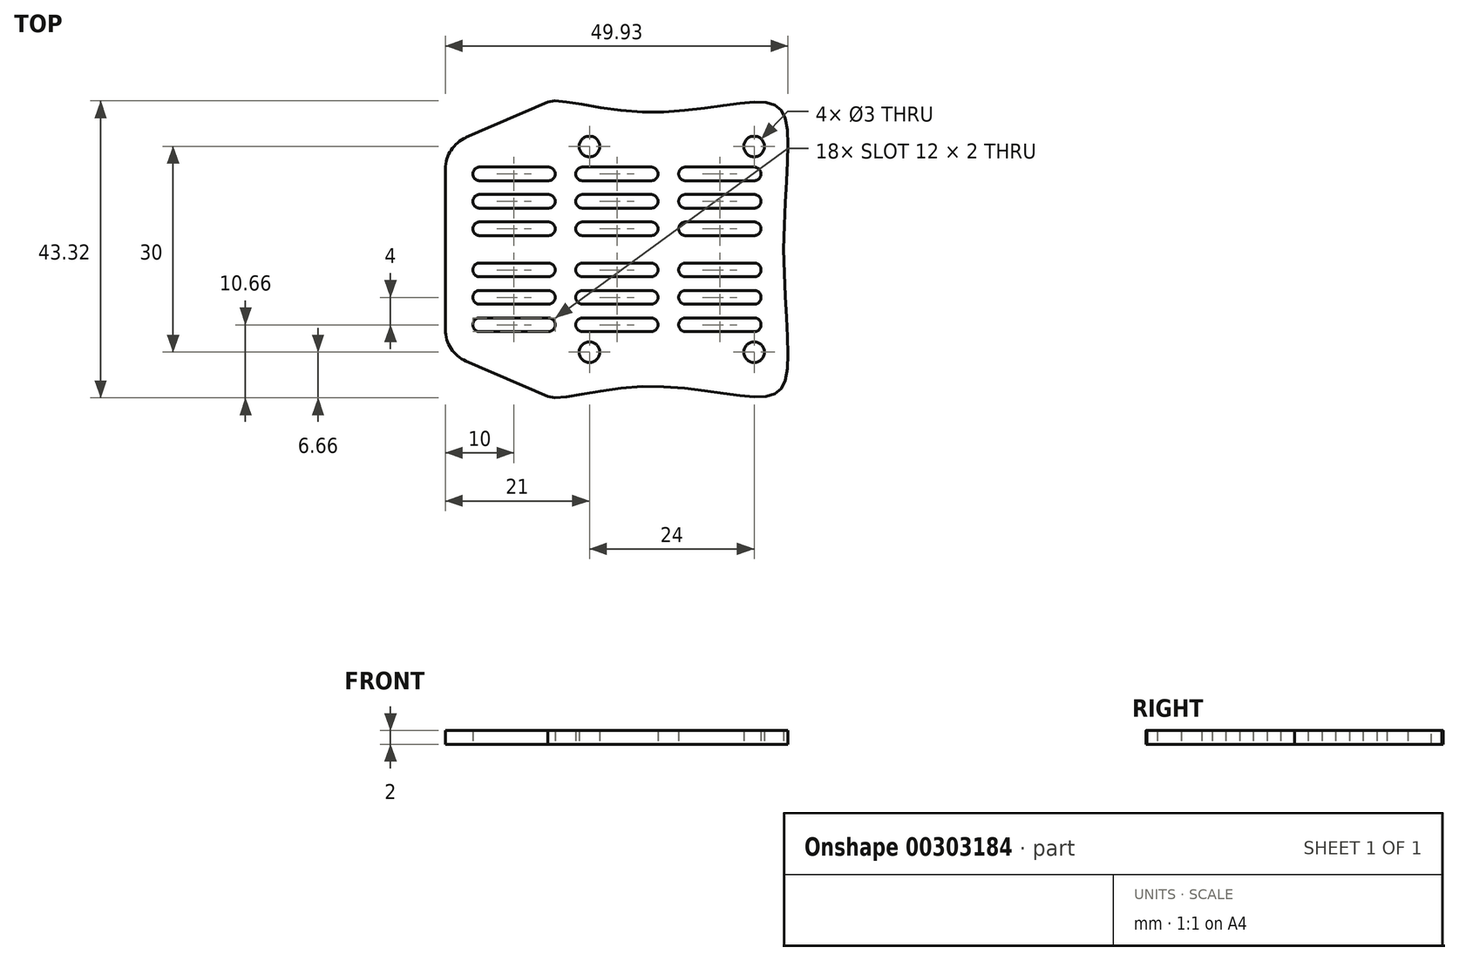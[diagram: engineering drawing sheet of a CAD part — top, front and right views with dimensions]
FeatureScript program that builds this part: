
annotation { "Feature Type Name" : "Feature", "Feature Type Description" : "" }
export const myFeature = defineFeature(function(context is Context, id is Id, definition is map)
    precondition{}
    {
        {
            var Q0;
            Q0=qCreatedBy(makeId("Top.planeOp"),FACE);
            var sketch = newSketch(context, id + "F0", { "sketchPlane" : qUnion([Q0])});
            skLineSegment(sketch, "E0", {"start": v(0, 0) * mm, "end": v(0, -11.72) * mm});
            skLineSegment(sketch, "E1", {"start": v(3.01, -16.3) * mm, "end": v(14.91, -21.46) * mm});
            skPoint(sketch, "E2.visualSharp", {"position": v(0, -15) * mm});
            skArc(sketch, "E2.filletArc", {"start": v(0, -11.72) * mm, "mid": v(0.82, -14.46) * mm, "end": v(3.01, -16.3) * mm});
            skCircle(sketch, "E3", {"center": v(45, -15) * mm, "radius": 1.5 * mm});
            skCircle(sketch, "E4", {"center": v(21, -15) * mm, "radius": 1.5 * mm});
            skLineSegment(sketch, "E5", {"start": v(0, -20) * mm, "end": v(69.47, -20) * mm, "construction": true});
            skLineSegment(sketch, "E6.MirrorCS", {"start": v(0, 20) * mm, "end": v(69.47, 20) * mm, "construction": true});
            skFitSpline(sketch, "E7", {"points": [v(14.91, -21.46) * mm, v(28.67, -20) * mm, v(46.46, -21.46) * mm, v(49.49, -19.15) * mm, v(49.31, 0) * mm], "startDerivative": vector(14.2, -9.6) * mm, "endDerivative": vector(-0.82, 81.71) * mm});
            skLineSegment(sketch, "E8.MirrorCS", {"start": v(0, 0) * mm, "end": v(0, 11.72) * mm});
            skArc(sketch, "E9.MirrorCS", {"start": v(0, 11.72) * mm, "mid": v(0.82, 14.46) * mm, "end": v(3.01, 16.3) * mm});
            skLineSegment(sketch, "E10.MirrorCS", {"start": v(3.01, 16.3) * mm, "end": v(14.91, 21.46) * mm});
            skFitSpline(sketch, "E11.MirrorCS", {"points": [v(14.91, 21.46) * mm, v(28.67, 20) * mm, v(46.46, 21.46) * mm, v(49.49, 19.15) * mm, v(49.31, 0) * mm], "startDerivative": vector(14.2, 9.6) * mm, "endDerivative": vector(-0.82, -81.71) * mm});
            skCircle(sketch, "E12.MirrorC", {"center": v(45, 15) * mm, "radius": 1.5 * mm});
            skCircle(sketch, "E13.MirrorC", {"center": v(21, 15) * mm, "radius": 1.5 * mm});
            skLineSegment(sketch, "E14", {"start": v(5, -3) * mm, "end": v(15, -3) * mm, "construction": true});
            skArc(sketch, "E15.0.startCap", {"start": v(5, -4) * mm, "mid": v(4, -3) * mm, "end": v(5, -2) * mm});
            skArc(sketch, "E15.0.endCap", {"start": v(15, -2) * mm, "mid": v(16, -3) * mm, "end": v(15, -4) * mm});
            skLineSegment(sketch, "E15.0.left", {"start": v(5, -2) * mm, "end": v(15, -2) * mm});
            skLineSegment(sketch, "E15.0.right", {"start": v(5, -4) * mm, "end": v(15, -4) * mm});
            skLineSegment(sketch, "E16.0.1.0", {"start": v(5, -8) * mm, "end": v(15, -8) * mm});
            skArc(sketch, "E16.0.1.1", {"start": v(15, -6) * mm, "mid": v(16, -7) * mm, "end": v(15, -8) * mm});
            skLineSegment(sketch, "E16.0.1.2", {"start": v(5, -6) * mm, "end": v(15, -6) * mm});
            skArc(sketch, "E16.0.1.3", {"start": v(5, -8) * mm, "mid": v(4, -7) * mm, "end": v(5, -6) * mm});
            skLineSegment(sketch, "E16.0.2.0", {"start": v(5, -12) * mm, "end": v(15, -12) * mm});
            skArc(sketch, "E16.0.2.1", {"start": v(15, -10) * mm, "mid": v(16, -11) * mm, "end": v(15, -12) * mm});
            skLineSegment(sketch, "E16.0.2.2", {"start": v(5, -10) * mm, "end": v(15, -10) * mm});
            skArc(sketch, "E16.0.2.3", {"start": v(5, -12) * mm, "mid": v(4, -11) * mm, "end": v(5, -10) * mm});
            skLineSegment(sketch, "E16.1.0.0", {"start": v(20, -4) * mm, "end": v(30, -4) * mm});
            skArc(sketch, "E16.1.0.1", {"start": v(30, -2) * mm, "mid": v(31, -3) * mm, "end": v(30, -4) * mm});
            skLineSegment(sketch, "E16.1.0.2", {"start": v(20, -2) * mm, "end": v(30, -2) * mm});
            skArc(sketch, "E16.1.0.3", {"start": v(20, -4) * mm, "mid": v(19, -3) * mm, "end": v(20, -2) * mm});
            skLineSegment(sketch, "E16.1.1.0", {"start": v(20, -8) * mm, "end": v(30, -8) * mm});
            skArc(sketch, "E16.1.1.1", {"start": v(30, -6) * mm, "mid": v(31, -7) * mm, "end": v(30, -8) * mm});
            skLineSegment(sketch, "E16.1.1.2", {"start": v(20, -6) * mm, "end": v(30, -6) * mm});
            skArc(sketch, "E16.1.1.3", {"start": v(20, -8) * mm, "mid": v(19, -7) * mm, "end": v(20, -6) * mm});
            skLineSegment(sketch, "E16.1.2.0", {"start": v(20, -12) * mm, "end": v(30, -12) * mm});
            skArc(sketch, "E16.1.2.1", {"start": v(30, -10) * mm, "mid": v(31, -11) * mm, "end": v(30, -12) * mm});
            skLineSegment(sketch, "E16.1.2.2", {"start": v(20, -10) * mm, "end": v(30, -10) * mm});
            skArc(sketch, "E16.1.2.3", {"start": v(20, -12) * mm, "mid": v(19, -11) * mm, "end": v(20, -10) * mm});
            skLineSegment(sketch, "E16.2.0.0", {"start": v(35, -4) * mm, "end": v(45, -4) * mm});
            skArc(sketch, "E16.2.0.1", {"start": v(45, -2) * mm, "mid": v(46, -3) * mm, "end": v(45, -4) * mm});
            skLineSegment(sketch, "E16.2.0.2", {"start": v(35, -2) * mm, "end": v(45, -2) * mm});
            skArc(sketch, "E16.2.0.3", {"start": v(35, -4) * mm, "mid": v(34, -3) * mm, "end": v(35, -2) * mm});
            skLineSegment(sketch, "E16.2.1.0", {"start": v(35, -8) * mm, "end": v(45, -8) * mm});
            skArc(sketch, "E16.2.1.1", {"start": v(45, -6) * mm, "mid": v(46, -7) * mm, "end": v(45, -8) * mm});
            skLineSegment(sketch, "E16.2.1.2", {"start": v(35, -6) * mm, "end": v(45, -6) * mm});
            skArc(sketch, "E16.2.1.3", {"start": v(35, -8) * mm, "mid": v(34, -7) * mm, "end": v(35, -6) * mm});
            skLineSegment(sketch, "E16.2.2.0", {"start": v(35, -12) * mm, "end": v(45, -12) * mm});
            skArc(sketch, "E16.2.2.1", {"start": v(45, -10) * mm, "mid": v(46, -11) * mm, "end": v(45, -12) * mm});
            skLineSegment(sketch, "E16.2.2.2", {"start": v(35, -10) * mm, "end": v(45, -10) * mm});
            skArc(sketch, "E16.2.2.3", {"start": v(35, -12) * mm, "mid": v(34, -11) * mm, "end": v(35, -10) * mm});
            skLineSegment(sketch, "E16.direction1", {"start": v(5, -4) * mm, "end": v(20, -4) * mm, "construction": true});
            skLineSegment(sketch, "E16.direction2", {"start": v(5, -4) * mm, "end": v(5, -8) * mm, "construction": true});
            skLineSegment(sketch, "E17.MirrorCS", {"start": v(5, 4) * mm, "end": v(15, 4) * mm});
            skLineSegment(sketch, "E18.MirrorCS", {"start": v(20, 6) * mm, "end": v(30, 6) * mm});
            skArc(sketch, "E19.MirrorCS", {"start": v(15, 10) * mm, "mid": v(16, 11) * mm, "end": v(15, 12) * mm});
            skArc(sketch, "E20.MirrorCS", {"start": v(20, 4) * mm, "mid": v(19, 3) * mm, "end": v(20, 2) * mm});
            skArc(sketch, "E21.MirrorCS", {"start": v(45, 2) * mm, "mid": v(46, 3) * mm, "end": v(45, 4) * mm});
            skArc(sketch, "E22.MirrorCS", {"start": v(30, 6) * mm, "mid": v(31, 7) * mm, "end": v(30, 8) * mm});
            skArc(sketch, "E23.MirrorCS", {"start": v(45, 10) * mm, "mid": v(46, 11) * mm, "end": v(45, 12) * mm});
            skLineSegment(sketch, "E24.MirrorCS", {"start": v(5, 3) * mm, "end": v(15, 3) * mm, "construction": true});
            skArc(sketch, "E25.MirrorCS", {"start": v(20, 12) * mm, "mid": v(19, 11) * mm, "end": v(20, 10) * mm});
            skLineSegment(sketch, "E26.MirrorCS", {"start": v(5, 8) * mm, "end": v(15, 8) * mm});
            skArc(sketch, "E27.MirrorCS", {"start": v(15, 2) * mm, "mid": v(16, 3) * mm, "end": v(15, 4) * mm});
            skArc(sketch, "E28.MirrorCS", {"start": v(15, 6) * mm, "mid": v(16, 7) * mm, "end": v(15, 8) * mm});
            skArc(sketch, "E29.MirrorCS", {"start": v(35, 4) * mm, "mid": v(34, 3) * mm, "end": v(35, 2) * mm});
            skLineSegment(sketch, "E30.MirrorCS", {"start": v(20, 2) * mm, "end": v(30, 2) * mm});
            skArc(sketch, "E31.MirrorCS", {"start": v(30, 10) * mm, "mid": v(31, 11) * mm, "end": v(30, 12) * mm});
            skLineSegment(sketch, "E32.MirrorCS", {"start": v(5, 12) * mm, "end": v(15, 12) * mm});
            skArc(sketch, "E33.MirrorCS", {"start": v(30, 2) * mm, "mid": v(31, 3) * mm, "end": v(30, 4) * mm});
            skLineSegment(sketch, "E34.MirrorCS", {"start": v(20, 10) * mm, "end": v(30, 10) * mm});
            skLineSegment(sketch, "E35.MirrorCS", {"start": v(20, 8) * mm, "end": v(30, 8) * mm});
            skLineSegment(sketch, "E36.MirrorCS", {"start": v(35, 12) * mm, "end": v(45, 12) * mm});
            skArc(sketch, "E37.MirrorCS", {"start": v(5, 4) * mm, "mid": v(4, 3) * mm, "end": v(5, 2) * mm});
            skArc(sketch, "E38.MirrorCS", {"start": v(5, 8) * mm, "mid": v(4, 7) * mm, "end": v(5, 6) * mm});
            skLineSegment(sketch, "E39.MirrorCS", {"start": v(20, 12) * mm, "end": v(30, 12) * mm});
            skArc(sketch, "E40.MirrorCS", {"start": v(35, 8) * mm, "mid": v(34, 7) * mm, "end": v(35, 6) * mm});
            skArc(sketch, "E41.MirrorCS", {"start": v(5, 12) * mm, "mid": v(4, 11) * mm, "end": v(5, 10) * mm});
            skArc(sketch, "E42.MirrorCS", {"start": v(45, 6) * mm, "mid": v(46, 7) * mm, "end": v(45, 8) * mm});
            skLineSegment(sketch, "E43.MirrorCS", {"start": v(5, 6) * mm, "end": v(15, 6) * mm});
            skLineSegment(sketch, "E44.MirrorCS", {"start": v(20, 4) * mm, "end": v(30, 4) * mm});
            skLineSegment(sketch, "E45.MirrorCS", {"start": v(35, 8) * mm, "end": v(45, 8) * mm});
            skArc(sketch, "E46.MirrorCS", {"start": v(20, 8) * mm, "mid": v(19, 7) * mm, "end": v(20, 6) * mm});
            skArc(sketch, "E47.MirrorCS", {"start": v(35, 12) * mm, "mid": v(34, 11) * mm, "end": v(35, 10) * mm});
            skLineSegment(sketch, "E48.MirrorCS", {"start": v(5, 10) * mm, "end": v(15, 10) * mm});
            skLineSegment(sketch, "E49.MirrorCS", {"start": v(35, 2) * mm, "end": v(45, 2) * mm});
            skLineSegment(sketch, "E50.MirrorCS", {"start": v(5, 4) * mm, "end": v(5, 8) * mm, "construction": true});
            skLineSegment(sketch, "E51.MirrorCS", {"start": v(5, 4) * mm, "end": v(20, 4) * mm, "construction": true});
            skLineSegment(sketch, "E52.MirrorCS", {"start": v(35, 10) * mm, "end": v(45, 10) * mm});
            skLineSegment(sketch, "E53.MirrorCS", {"start": v(5, 2) * mm, "end": v(15, 2) * mm});
            skLineSegment(sketch, "E54.MirrorCS", {"start": v(35, 4) * mm, "end": v(45, 4) * mm});
            skLineSegment(sketch, "E55.MirrorCS", {"start": v(35, 6) * mm, "end": v(45, 6) * mm});
            skSolve(sketch);
        }
        {
            var Q0;
            Q0=makeQuery(id+"F0.imprint","IMPRINT",FACE,{"disambiguationData":[TD([[makeQuery(id+"F0.imprint","IMPRINT",EDGE,{"derivedFrom":sQuery(id+"F0.wireOp",EDGE,"E0")}),1.0]])]});
            extrude(context, id + "F1", {"entities" : qUnion([Q0]), "depth" : 2 * mm});
        }
    });
